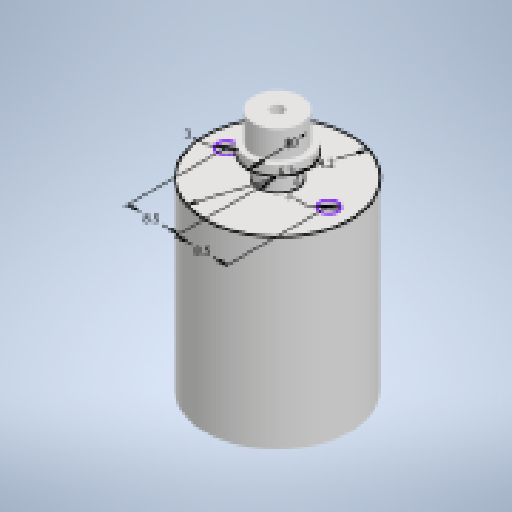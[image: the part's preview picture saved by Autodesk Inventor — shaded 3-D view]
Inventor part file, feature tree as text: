
AUTODESK INVENTOR PART (.ipt)
format: ipt  version: 2023.1 (Build 271208000, 208)  size: 166,400 bytes
history: native  units: in
note: dims shown in document units (in); Inventor stores cm internally (conversion verified against a paired STEP export)
features: extrude x6, sketch x2, plane x1
ambient origin geometry x8: Origin, YZ Plane, XZ Plane, XY Plane, X Axis, Y Axis, Z Axis, Center Point
bodies: Solid1 (feature_tree)
feature tree (9):
  sketch  "Sketch1"  dims[d0=0.9528in d1=0.248in]
  extrude  "Extrusion1"  Depth=0.248in
  extrude  "Extrusion2"  Depth=0.0787in TaperAngle=0.0deg
  extrude  "Extrusion3"  Depth=0.0787in
  plane  "Work Plane1"
  sketch  "Sketch2"  dims[d2=1.2087in d3=0.0in d4=0.0787in d5=0.0in d6=0.0787in d7=0.3346in d8=0.0in d9=-0.1875in d10=0.3937in d11=0.315in d12=0.0591in d13=0.0in d14=0.2362in d15=0.0in d16=0.1181in d17=0.1181in d18=0.3346in d19=0.3346in d20=0.1969in d21=0.0in]
  extrude  "Extrusion4"  Depth=0.3346in TaperAngle=0.0deg
  extrude  "Extrusion5"  [1 undecoded]
  extrude  "Extrusion6"  Depth=0.3937in
note: 1 required parameter value undecoded (feature->parameter linkage not recoverable at this tier; creation-order binding heuristic only, values carry confidence <= 0.55)
